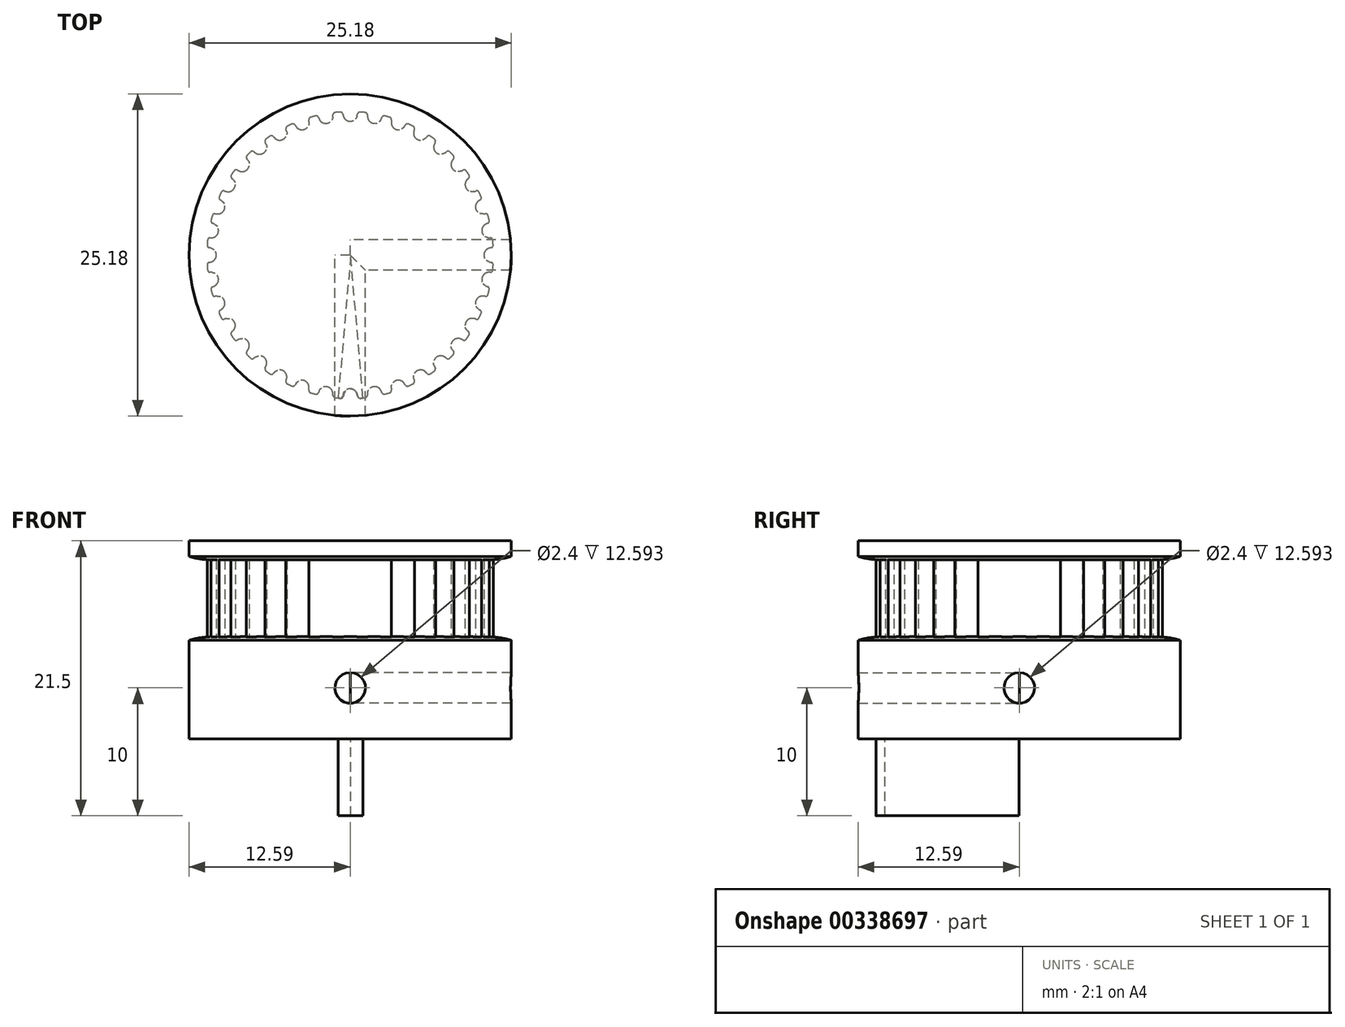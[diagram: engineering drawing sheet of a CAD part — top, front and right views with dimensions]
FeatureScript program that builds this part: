
annotation { "Feature Type Name" : "Feature", "Feature Type Description" : "" }
export const myFeature = defineFeature(function(context is Context, id is Id, definition is map)
    precondition{}
    {
        {
            assignVariable(context, id + "F0", {"name" : "teeth", "anyValue" : 36});
        }
        {
            assignVariable(context, id + "F1", {"name" : "belt_width", "anyValue" : 6 * mm});
        }
        {
            var Q0;
            Q0=qCreatedBy(makeId("Top.planeOp"),FACE);
            var sketch = newSketch(context, id + "F2", { "sketchPlane" : qUnion([Q0])});
            skLineSegment(sketch, "E0", {"start": v(0, 0) * mm, "end": v(0, 10.46) * mm, "construction": true});
            skCircle(sketch, "E1", {"center": v(0, 0) * mm, "radius": 11.2 * mm});
            skPoint(sketch, "E2.MirrorCS.end.orphan", {"position": v(0.98, 11.16) * mm});
            skLineSegment(sketch, "E3", {"start": v(0.98, 11.16) * mm, "end": v(1, 11.42) * mm, "construction": true});
            skLineSegment(sketch, "E4", {"start": v(-0.98, 11.16) * mm, "end": v(-1, 11.42) * mm, "construction": true});
            skArc(sketch, "E5", {"start": v(0, 10.46) * mm, "mid": v(0.34, 10.57) * mm, "end": v(0.53, 10.86) * mm});
            skArc(sketch, "E6", {"start": v(0.53, 10.86) * mm, "mid": v(0.56, 10.96) * mm, "end": v(0.58, 11.05) * mm, "construction": true});
            skLineSegment(sketch, "E7", {"start": v(0, 10.46) * mm, "end": v(0, 11.2) * mm, "construction": true});
            skLineSegment(sketch, "E8", {"start": v(0, 11.2) * mm, "end": v(0, 11.46) * mm, "construction": true});
            skArc(sketch, "E9", {"start": v(0.58, 11.05) * mm, "mid": v(0.64, 11.15) * mm, "end": v(0.74, 11.18) * mm, "construction": true});
            skArc(sketch, "E10", {"start": v(1, 11.42) * mm, "mid": v(0, 11.46) * mm, "end": v(-1, 11.42) * mm, "construction": true});
            skLineSegment(sketch, "E11", {"start": v(0.98, 11.16) * mm, "end": v(0.91, 10.42) * mm});
            skLineSegment(sketch, "E12", {"start": v(0.91, 10.42) * mm, "end": v(0, 0) * mm});
            skLineSegment(sketch, "E13", {"start": v(0, 0) * mm, "end": v(-0.91, 10.42) * mm});
            skLineSegment(sketch, "E14", {"start": v(-0.91, 10.42) * mm, "end": v(-0.98, 11.16) * mm});
            skArc(sketch, "E15", {"start": v(0.78, 11.18) * mm, "mid": v(0.65, 11.14) * mm, "end": v(0.58, 11.04) * mm});
            skArc(sketch, "E16", {"start": v(0.53, 10.86) * mm, "mid": v(0.56, 10.95) * mm, "end": v(0.58, 11.04) * mm});
            skArc(sketch, "E17.MirrorCS", {"start": v(0, 10.46) * mm, "mid": v(-0.34, 10.57) * mm, "end": v(-0.53, 10.86) * mm});
            skArc(sketch, "E18.MirrorCS", {"start": v(-0.53, 10.86) * mm, "mid": v(-0.56, 10.95) * mm, "end": v(-0.58, 11.04) * mm});
            skArc(sketch, "E19.MirrorCS", {"start": v(-0.78, 11.18) * mm, "mid": v(-0.65, 11.14) * mm, "end": v(-0.58, 11.04) * mm});
            skArc(sketch, "E20", {"start": v(0, 11.2) * mm, "mid": v(-0.2, 11.2) * mm, "end": v(-0.4, 11.2) * mm});
            skArc(sketch, "E21", {"start": v(0.91, 10.42) * mm, "mid": v(0, 10.46) * mm, "end": v(-0.91, 10.42) * mm, "construction": true});
            skLineSegment(sketch, "E22", {"start": v(1, 11.42) * mm, "end": v(1.03, 11.8) * mm, "construction": true});
            skLineSegment(sketch, "E23", {"start": v(-1, 11.42) * mm, "end": v(-1.03, 11.8) * mm, "construction": true});
            skArc(sketch, "E24", {"start": v(-1.03, 11.8) * mm, "mid": v(0, 11.84) * mm, "end": v(1.03, 11.8) * mm, "construction": true});
            skSolve(sketch);
        }
        {
            var Q0;
            Q0=makeQuery(id+"F2.imprint","IMPRINT",FACE,{"disambiguationData":[TD([[makeQuery(id+"F2.imprint","IMPRINT",EDGE,{"derivedFrom":sQuery(id+"F2.wireOp",EDGE,"E5")}),-1.0]])]});
            var Q1;
            {var subQ1=sQuery(id+"F2.wireOp",EDGE,"E14");Q1=makeQuery(id+"F2.imprint","IMPRINT",FACE,{"disambiguationData":[TD([[makeQuery(id+"F2.imprint","IMPRINT",EDGE,{"derivedFrom":subQ1}),-1.0]])]});}
            var Q2;
            {var subQ0=sQuery(id+"F2.wireOp",EDGE,"E12");Q2=makeQuery(id+"F2.imprint","IMPRINT",FACE,{"disambiguationData":[TD([[makeQuery(id+"F2.imprint","IMPRINT",EDGE,{"derivedFrom":subQ0}),-1.0]])]});}
            extrude(context, id + "F3", {"entities" : qUnion([Q0, Q1, Q2]), "endBound" : BoundingType.SYMMETRIC, "depth" : getVariable(context, 'belt_width')});
        }
        {
            var Q0;
            Q0=makeQuery(id+"F3.opExtrude","SWEPT_BODY",BODY,{"disambiguationData":[OSD([sQuery(id+"F2.wireOp",EDGE,"E1"),sQuery(id+"F2.wireOp",EDGE,"E5"),sQuery(id+"F2.wireOp",EDGE,"E11"),sQuery(id+"F2.wireOp",EDGE,"E12"),sQuery(id+"F2.wireOp",EDGE,"E13"),sQuery(id+"F2.wireOp",EDGE,"E14"),sQuery(id+"F2.wireOp",EDGE,"E15"),sQuery(id+"F2.wireOp",EDGE,"E16"),sQuery(id+"F2.wireOp",EDGE,"E17.MirrorCS"),sQuery(id+"F2.wireOp",EDGE,"E18.MirrorCS"),sQuery(id+"F2.wireOp",EDGE,"E19.MirrorCS")])]});
            var Q1;
            Q1=makeQuery(id+"F3.opExtrude","SWEPT_EDGE",EDGE,{"disambiguationData":[OSD([sQuery(id+"F2.wireOp",EDGE,"E12"),sQuery(id+"F2.wireOp",EDGE,"E13")])]});
            circularPattern(context, id + "F4", {"operationType" : NewBodyOperationType.ADD, "entities" : qUnion([Q0]), "axis" : qUnion([Q1]), "angle" : 360 * degree, "instanceCount" : getVariable(context, 'teeth'), "equalSpace" : true});
        }
        {
            var Q0;
            Q0=qCreatedBy(makeId("Front.planeOp"),FACE);
            var sketch = newSketch(context, id + "F5", { "sketchPlane" : qUnion([Q0])});
            skLineSegment(sketch, "E25", {"start": v(0, -3) * mm, "end": v(11.84, -3) * mm});
            skLineSegment(sketch, "E26", {"start": v(11.84, -3) * mm, "end": v(12.6, -3.28) * mm});
            skLineSegment(sketch, "E27", {"start": v(12.6, -3.28) * mm, "end": v(12.6, -11) * mm});
            skLineSegment(sketch, "E28", {"start": v(12.6, -11) * mm, "end": v(0, -11) * mm});
            skLineSegment(sketch, "E29", {"start": v(0, -11) * mm, "end": v(0, -3) * mm});
            skLineSegment(sketch, "E30", {"start": v(0, 3) * mm, "end": v(11.84, 3) * mm});
            skLineSegment(sketch, "E31", {"start": v(12.6, 3.28) * mm, "end": v(11.84, 3) * mm});
            skLineSegment(sketch, "E32", {"start": v(12.6, 3.28) * mm, "end": v(12.6, 4.5) * mm});
            skLineSegment(sketch, "E33", {"start": v(12.6, 4.5) * mm, "end": v(0, 4.5) * mm});
            skLineSegment(sketch, "E34", {"start": v(0, 4.5) * mm, "end": v(0, 3) * mm});
            skLineSegment(sketch, "E35", {"start": v(11.84, -3) * mm, "end": v(12.6, -3) * mm, "construction": true});
            skLineSegment(sketch, "E36", {"start": v(12.6, -3) * mm, "end": v(12.6, -3.28) * mm, "construction": true});
            skLineSegment(sketch, "E37", {"start": v(11.84, 3) * mm, "end": v(12.6, 3) * mm, "construction": true});
            skLineSegment(sketch, "E38", {"start": v(12.6, 3) * mm, "end": v(12.6, 3.28) * mm, "construction": true});
            skLineSegment(sketch, "E39", {"start": v(11.2, 0) * mm, "end": v(11.2, -3) * mm, "construction": true});
            skSolve(sketch);
        }
        {
            var Q0;
            Q0=qSketchRegion(id+"F5",true);
            var Q1;
            Q1=qConstructionFilter(qBodyType(qCreatedBy(id+"F5",EDGE),BodyType.WIRE),ConstructionObject.NO);
            var Q2;
            Q2=sQuery(id+"F5.wireOp",EDGE,"E29");
            revolve(context, id + "F6", {"operationType" : NewBodyOperationType.ADD, "entities" : qUnion([Q0]), "surfaceEntities" : qUnion([Q1]), "axis" : qUnion([Q2]), "revolveType" : RevolveType.FULL});
        }
        {
            var Q0;
            Q0=qCreatedBy(makeId("Front.planeOp"),FACE);
            var sketch = newSketch(context, id + "F7", { "sketchPlane" : qUnion([Q0])});
            skPoint(sketch, "E40", {"position": v(0, -7) * mm});
            skLineSegment(sketch, "E41", {"start": v(0, -11) * mm, "end": v(0, -3) * mm});
            skSolve(sketch);
        }
        {
            var Q0;
            Q0=qCreatedBy(makeId("Right.planeOp"),FACE);
            var sketch = newSketch(context, id + "F8", { "sketchPlane" : qUnion([Q0])});
            skPoint(sketch, "E42", {"position": v(0, -7) * mm});
            skSolve(sketch);
        }
        {
            var Q0;
            Q0=sQuery(id+"F7.wireOp",VERTEX,"E40");
            var Q1;
            Q1=makeQuery(id+"F3.opExtrude","SWEPT_BODY",BODY,{"disambiguationData":[OSD([sQuery(id+"F2.wireOp",EDGE,"E1"),sQuery(id+"F2.wireOp",EDGE,"E5"),sQuery(id+"F2.wireOp",EDGE,"E11"),sQuery(id+"F2.wireOp",EDGE,"E12"),sQuery(id+"F2.wireOp",EDGE,"E13"),sQuery(id+"F2.wireOp",EDGE,"E14"),sQuery(id+"F2.wireOp",EDGE,"E15"),sQuery(id+"F2.wireOp",EDGE,"E16"),sQuery(id+"F2.wireOp",EDGE,"E17.MirrorCS"),sQuery(id+"F2.wireOp",EDGE,"E18.MirrorCS"),sQuery(id+"F2.wireOp",EDGE,"E19.MirrorCS")])]});
            hole(context, id + "F9", {"style" : HoleStyle.SIMPLE, "endStyle" : HoleEndStyle.THROUGH, "oppositeDirection" : true, "standardTappedOrClearance" : lookupTablePath({ "standard" : "ISO", "engagement" : "75%", "pitch" : "0.6 mm", "size" : "M3", "type" : "Tapped" }), "standardBlindInLast" : lookupTablePath({ "standard" : "ISO", "engagement" : "75%", "pitch" : "0.6 mm", "size" : "M3", "type" : "Tapped" }), "holeDiameter" : 2.4 * mm, "locations" : qUnion([Q0]), "scope" : qUnion([Q1]), "isTappedThrough" : true, "showTappedDepth" : true});
        }
        {
            var Q0;
            Q0=sQuery(id+"F8.wireOp",VERTEX,"E42");
            var Q1;
            Q1=makeQuery(id+"F3.opExtrude","SWEPT_BODY",BODY,{"disambiguationData":[OSD([sQuery(id+"F2.wireOp",EDGE,"E1"),sQuery(id+"F2.wireOp",EDGE,"E5"),sQuery(id+"F2.wireOp",EDGE,"E11"),sQuery(id+"F2.wireOp",EDGE,"E12"),sQuery(id+"F2.wireOp",EDGE,"E13"),sQuery(id+"F2.wireOp",EDGE,"E14"),sQuery(id+"F2.wireOp",EDGE,"E15"),sQuery(id+"F2.wireOp",EDGE,"E16"),sQuery(id+"F2.wireOp",EDGE,"E17.MirrorCS"),sQuery(id+"F2.wireOp",EDGE,"E18.MirrorCS"),sQuery(id+"F2.wireOp",EDGE,"E19.MirrorCS")])]});
            hole(context, id + "F10", {"style" : HoleStyle.SIMPLE, "endStyle" : HoleEndStyle.THROUGH, "oppositeDirection" : true, "standardTappedOrClearance" : lookupTablePath({ "standard" : "ISO", "engagement" : "75%", "pitch" : "0.6 mm", "size" : "M3", "type" : "Tapped" }), "standardBlindInLast" : lookupTablePath({ "standard" : "ISO", "engagement" : "75%", "pitch" : "0.6 mm", "size" : "M3", "type" : "Tapped" }), "holeDiameter" : 2.4 * mm, "locations" : qUnion([Q0]), "scope" : qUnion([Q1]), "isTappedThrough" : true, "showTappedDepth" : true});
        }
        {
            var Q0;
            Q0=makeQuery(id+"F6.opRevolve","SWEPT_EDGE",EDGE,{"disambiguationData":[OSD([sQuery(id+"F5.wireOp",EDGE,"E25"),sQuery(id+"F5.wireOp",EDGE,"E26")])]});
            fillet(context, id + "F11", {"entities" : qUnion([Q0]), "radius" : 7 * mm, "tangentPropagation" : true, "allowEdgeOverflow" : false});
        }
        {
            var Q0;
            Q0=makeQuery(id+"F6.opRevolve","SWEPT_EDGE",EDGE,{"disambiguationData":[OSD([sQuery(id+"F5.wireOp",EDGE,"E30"),sQuery(id+"F5.wireOp",EDGE,"E31")])]});
            fillet(context, id + "F12", {"entities" : qUnion([Q0]), "radius" : 7 * mm, "tangentPropagation" : true, "allowEdgeOverflow" : false});
        }
        {
            var Q0;
            Q0=makeQuery(id+"F6.opRevolve","SWEPT_FACE",FACE,{"disambiguationData":[OSD([sQuery(id+"F5.wireOp",EDGE,"E28")])]});
            var sketch = newSketch(context, id + "F13", { "sketchPlane" : qUnion([Q0])});
            skLineSegment(sketch, "E43", {"start": v(0.04, 0.03) * mm, "end": v(0.04, 10.48) * mm, "construction": true});
            skCircle(sketch, "E44", {"center": v(0.04, 0.03) * mm, "radius": 11.2 * mm});
            skPoint(sketch, "E45.MirrorCS.end.orphan", {"position": v(1.01, 11.2) * mm});
            skLineSegment(sketch, "E46", {"start": v(1.01, 11.2) * mm, "end": v(1.03, 11.44) * mm, "construction": true});
            skLineSegment(sketch, "E47", {"start": v(-0.94, 11.2) * mm, "end": v(-0.96, 11.44) * mm, "construction": true});
            skArc(sketch, "E48", {"start": v(0.04, 10.48) * mm, "mid": v(0.37, 10.6) * mm, "end": v(0.57, 10.89) * mm});
            skArc(sketch, "E49", {"start": v(0.57, 10.89) * mm, "mid": v(0.6, 10.98) * mm, "end": v(0.62, 11.08) * mm, "construction": true});
            skLineSegment(sketch, "E50", {"start": v(0.04, 10.48) * mm, "end": v(0.04, 11.23) * mm, "construction": true});
            skLineSegment(sketch, "E51", {"start": v(0.04, 11.23) * mm, "end": v(0.04, 11.49) * mm, "construction": true});
            skArc(sketch, "E52", {"start": v(0.62, 11.08) * mm, "mid": v(0.67, 11.18) * mm, "end": v(0.78, 11.2) * mm, "construction": true});
            skArc(sketch, "E53", {"start": v(1.03, 11.44) * mm, "mid": v(0.04, 11.49) * mm, "end": v(-0.96, 11.44) * mm, "construction": true});
            skLineSegment(sketch, "E54", {"start": v(1.01, 11.2) * mm, "end": v(0.95, 10.44) * mm});
            skLineSegment(sketch, "E55", {"start": v(0.95, 10.44) * mm, "end": v(0.04, 0.03) * mm});
            skLineSegment(sketch, "E56", {"start": v(0.04, 0.03) * mm, "end": v(-0.88, 10.44) * mm});
            skLineSegment(sketch, "E57", {"start": v(-0.88, 10.44) * mm, "end": v(-0.94, 11.2) * mm});
            skArc(sketch, "E58", {"start": v(0.81, 11.2) * mm, "mid": v(0.69, 11.17) * mm, "end": v(0.62, 11.06) * mm});
            skArc(sketch, "E59", {"start": v(0.57, 10.89) * mm, "mid": v(0.6, 10.98) * mm, "end": v(0.62, 11.06) * mm});
            skArc(sketch, "E60.MirrorCS", {"start": v(0.04, 10.48) * mm, "mid": v(-0.3, 10.6) * mm, "end": v(-0.5, 10.89) * mm});
            skArc(sketch, "E61.MirrorCS", {"start": v(-0.5, 10.89) * mm, "mid": v(-0.52, 10.98) * mm, "end": v(-0.54, 11.06) * mm});
            skArc(sketch, "E62.MirrorCS", {"start": v(-0.74, 11.2) * mm, "mid": v(-0.62, 11.17) * mm, "end": v(-0.54, 11.06) * mm});
            skArc(sketch, "E63", {"start": v(0.04, 11.23) * mm, "mid": v(-0.17, 11.23) * mm, "end": v(-0.37, 11.23) * mm});
            skArc(sketch, "E64", {"start": v(0.95, 10.44) * mm, "mid": v(0.04, 10.48) * mm, "end": v(-0.88, 10.44) * mm, "construction": true});
            skLineSegment(sketch, "E65", {"start": v(1.03, 11.44) * mm, "end": v(1.07, 11.82) * mm, "construction": true});
            skLineSegment(sketch, "E66", {"start": v(-0.96, 11.44) * mm, "end": v(-1, 11.82) * mm, "construction": true});
            skArc(sketch, "E67", {"start": v(-1, 11.82) * mm, "mid": v(0.04, 11.86) * mm, "end": v(1.07, 11.82) * mm, "construction": true});
            skSolve(sketch);
        }
        {
            var Q0;
            Q0=makeQuery(id+"F13.imprint","IMPRINT",FACE,{"disambiguationData":[TD([[makeQuery(id+"F13.imprint","IMPRINT",EDGE,{"derivedFrom":sQuery(id+"F13.wireOp",EDGE,"E48")}),-1.0]])]});
            extrude(context, id + "F14", {"entities" : qUnion([Q0]), "operationType" : NewBodyOperationType.ADD, "depth" : 6 * mm});
        }
    });
